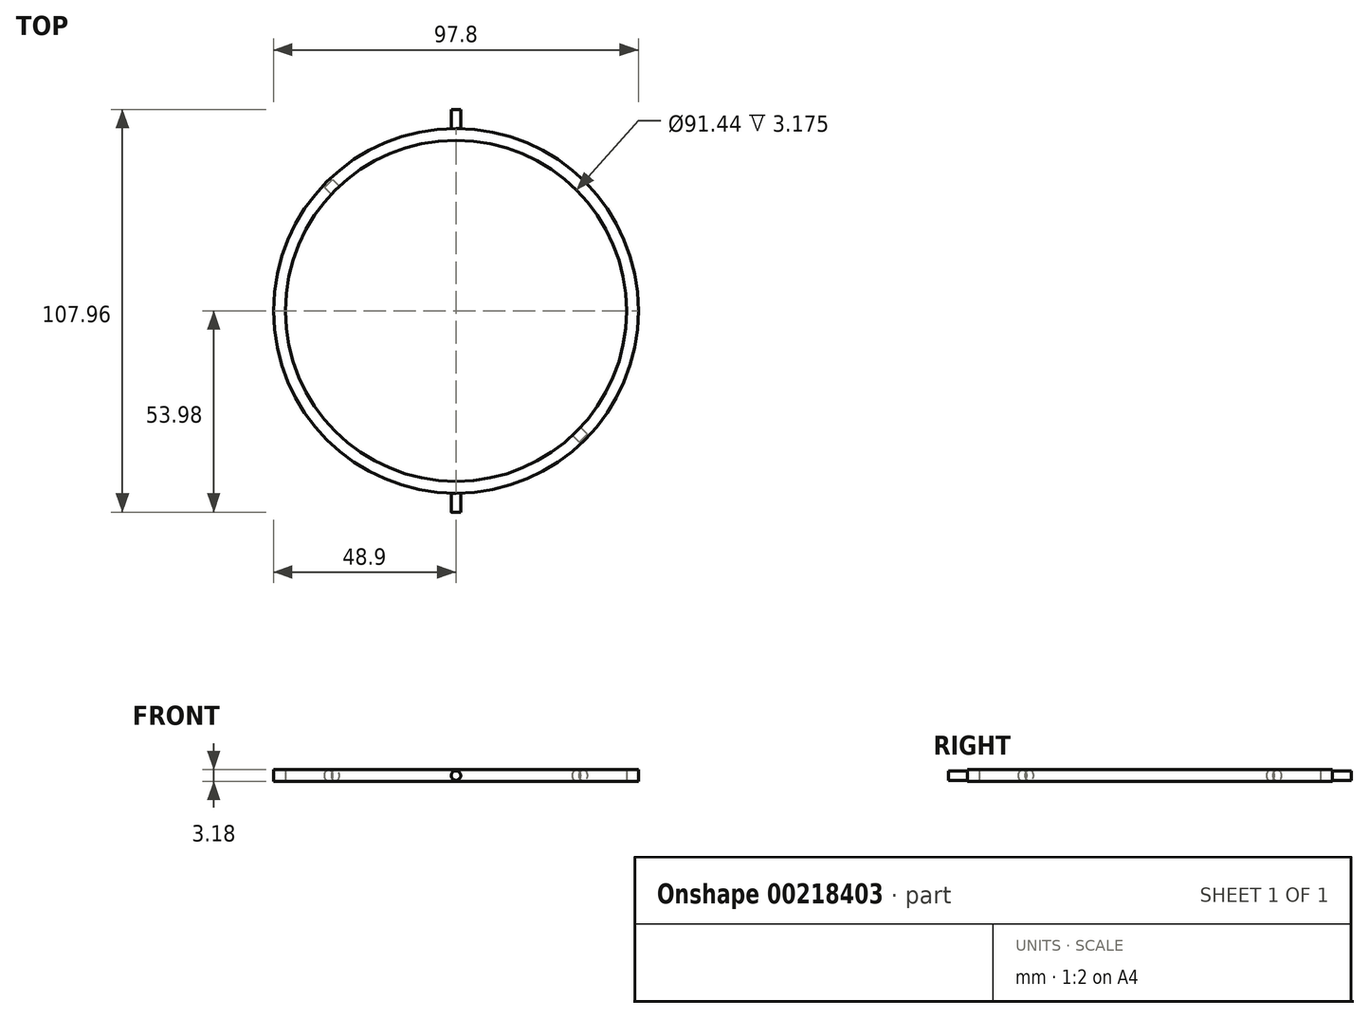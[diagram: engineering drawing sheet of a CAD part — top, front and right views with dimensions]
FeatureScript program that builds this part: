
annotation { "Feature Type Name" : "Feature", "Feature Type Description" : "" }
export const myFeature = defineFeature(function(context is Context, id is Id, definition is map)
    precondition{}
    {
        {
            var Q0;
            Q0=qCreatedBy(makeId("Top.planeOp"),FACE);
            var sketch = newSketch(context, id + "F0", { "sketchPlane" : qUnion([Q0])});
            skCircle(sketch, "E0", {"center": v(0, 0) * mm, "radius": 48.9 * mm});
            skCircle(sketch, "E1", {"center": v(0, 0) * mm, "radius": 45.72 * mm});
            skSolve(sketch);
        }
        {
            var Q0;
            Q0 = qSketchRegion(id + "F0", true);
            extrude(context, id + "F1", {"entities" : qUnion([Q0]), "depth" : 3.17 * mm});
        }
        {
            var Q0;
            Q0=qCreatedBy(makeId("Front.planeOp"),FACE);
            var sketch = newSketch(context, id + "F2", { "sketchPlane" : qUnion([Q0])});
            skLineSegment(sketch, "E2", {"start": v(0, 0) * mm, "end": v(0, 1.59) * mm, "construction": true});
            skCircle(sketch, "E3", {"center": v(0, 1.59) * mm, "radius": 1.27 * mm});
            skSolve(sketch);
        }
        {
            var Q0;
            Q0 = qSketchRegion(id + "F2", true);
            extrude(context, id + "F3", {"entities" : qUnion([Q0]), "operationType" : NewBodyOperationType.ADD, "depth" : 53.97 * mm, "hasSecondDirection" : true, "secondDirectionOppositeDirection" : true, "secondDirectionDepth" : 53.97 * mm});
        }
        {
            var Q0;
            Q0=qCreatedBy(makeId("Top.planeOp"),FACE);
            var sketch = newSketch(context, id + "F4", { "sketchPlane" : qUnion([Q0])});
            skCircle(sketch, "E4", {"center": v(0, 0) * mm, "radius": 45.72 * mm});
            skSolve(sketch);
        }
        {
            var Q0;
            Q0 = qSketchRegion(id + "F4", true);
            extrude(context, id + "F5", {"entities" : qUnion([Q0]), "operationType" : NewBodyOperationType.REMOVE, "depth" : 25.4 * mm});
        }
        {
            var Q0;
            Q0=qCreatedBy(makeId("Top.planeOp"),FACE);
            var sketch = newSketch(context, id + "F6", { "sketchPlane" : qUnion([Q0])});
            skLineSegment(sketch, "E5", {"start": v(0, 0) * mm, "end": v(29.65, 29.65) * mm, "construction": true});
            skSolve(sketch);
        }
        {
            var Q0;
            Q0=qCreatedBy(makeId("Front.planeOp"),FACE);
            var sketch = newSketch(context, id + "F7", { "sketchPlane" : qUnion([Q0])});
            skLineSegment(sketch, "E6", {"start": v(0, 0) * mm, "end": v(0, 33.09) * mm, "construction": true});
            skSolve(sketch);
        }
        {
            var Q0;
            Q0=sQuery(id+"F7.wireOp",EDGE,"E6");
            var Q1;
            Q1=sQuery(id+"F6.wireOp",EDGE,"E5");
            cPlane(context, id + "F8", {"entities" : qUnion([Q0, Q1]), "cplaneType" : CPlaneType.LINE_ANGLE, "offset" : 25.4 * mm, "angle" : 0 * degree, "width" : 152.4 * mm, "height" : 152.4 * mm});
        }
        {
            var Q0;
            Q0=qCreatedBy(id+"F8.planeOp",FACE);
            var sketch = newSketch(context, id + "F9", { "sketchPlane" : qUnion([Q0])});
            skLineSegment(sketch, "E7", {"start": v(0, 0) * mm, "end": v(0, 1.59) * mm, "construction": true});
            skCircle(sketch, "E8", {"center": v(0, 1.59) * mm, "radius": 1.52 * mm});
            skSolve(sketch);
        }
        {
            var Q0;
            Q0 = qSketchRegion(id + "F9", true);
            extrude(context, id + "F10", {"entities" : qUnion([Q0]), "operationType" : NewBodyOperationType.REMOVE, "oppositeDirection" : true, "depth" : 48.26 * mm, "hasSecondDirection" : true, "secondDirectionOppositeDirection" : false, "secondDirectionDepth" : 48.26 * mm});
        }
    });
